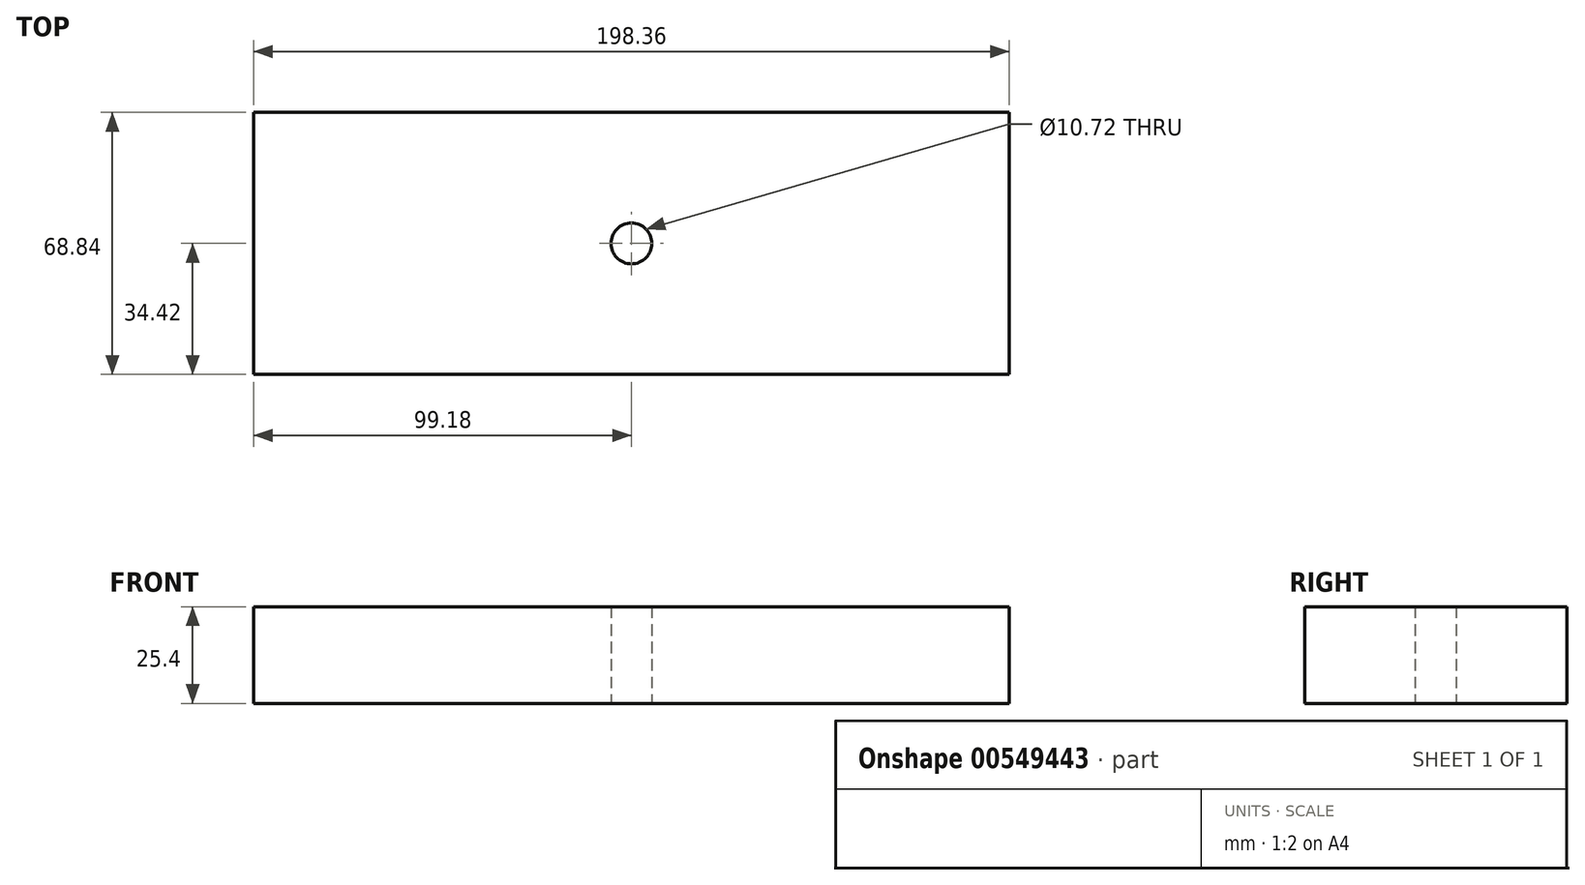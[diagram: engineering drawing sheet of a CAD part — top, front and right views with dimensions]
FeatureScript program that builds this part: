
annotation { "Feature Type Name" : "Feature", "Feature Type Description" : "" }
export const myFeature = defineFeature(function(context is Context, id is Id, definition is map)
    precondition{}
    {
        {
            var Q0;
            Q0=qCreatedBy(makeId("Top.planeOp"),FACE);
            var sketch = newSketch(context, id + "F0", { "sketchPlane" : qUnion([Q0])});
            skLineSegment(sketch, "E0.bottom", {"start": v(-99.18, 34.42) * mm, "end": v(99.18, 34.42) * mm});
            skLineSegment(sketch, "E0.top", {"start": v(-99.18, -34.42) * mm, "end": v(99.18, -34.42) * mm});
            skLineSegment(sketch, "E0.left", {"start": v(-99.18, 34.42) * mm, "end": v(-99.18, -34.42) * mm});
            skLineSegment(sketch, "E0.right", {"start": v(99.18, 34.42) * mm, "end": v(99.18, -34.42) * mm});
            skPoint(sketch, "E0.middle", {"position": v(0, 0) * mm});
            skSolve(sketch);
        }
        {
            var Q0;
            Q0 = qSketchRegion(id + "F0", true);
            extrude(context, id + "F1", {"entities" : qUnion([Q0]), "depth" : 25.4 * mm, "offsetDistance" : 25.4 * mm});
        }
        {
            var Q0;
            Q0=makeQuery(id+"F1.opExtrude","CAP_FACE",FACE,{"disambiguationData":[OSD([sQuery(id+"F0.wireOp",EDGE,"E0.bottom"),sQuery(id+"F0.wireOp",EDGE,"E0.top"),sQuery(id+"F0.wireOp",EDGE,"E0.left"),sQuery(id+"F0.wireOp",EDGE,"E0.right")])],"isStart":false});
            var sketch = newSketch(context, id + "F2", { "sketchPlane" : qUnion([Q0])});
            skPoint(sketch, "E1", {"position": v(0, 0) * mm});
            skSolve(sketch);
        }
        {
            var Q0;
            Q0=sQuery(id+"F2.wireOp",VERTEX,"E1");
            var Q1;
            Q1=makeQuery(id+"F1.opExtrude","SWEPT_BODY",BODY,{"disambiguationData":[OSD([sQuery(id+"F0.wireOp",EDGE,"E0.bottom"),sQuery(id+"F0.wireOp",EDGE,"E0.top"),sQuery(id+"F0.wireOp",EDGE,"E0.left"),sQuery(id+"F0.wireOp",EDGE,"E0.right")])]});
            hole(context, id + "F3", {"style" : HoleStyle.SIMPLE, "endStyle" : HoleEndStyle.BLIND, "standardTappedOrClearance" : lookupTablePath({ "standard" : "ANSI", "engagement" : "75%", "pitch" : "13 tpi", "size" : "1/2", "type" : "Tapped" }), "standardBlindInLast" : lookupTablePath({ "standard" : "ANSI", "engagement" : "75%", "pitch" : "13 tpi", "size" : "1/2", "type" : "Tapped" }), "holeDiameter" : 10.72 * mm, "majorDiameter" : 12.7 * mm, "showTappedDepth" : true, "holeDepth" : 50.32 * mm, "isTappedThrough" : true, "tappedDepth" : 44.46 * mm, "tapClearance" : 3, "startFromSketch" : true, "locations" : qUnion([Q0]), "scope" : qUnion([Q1])});
        }
    });
